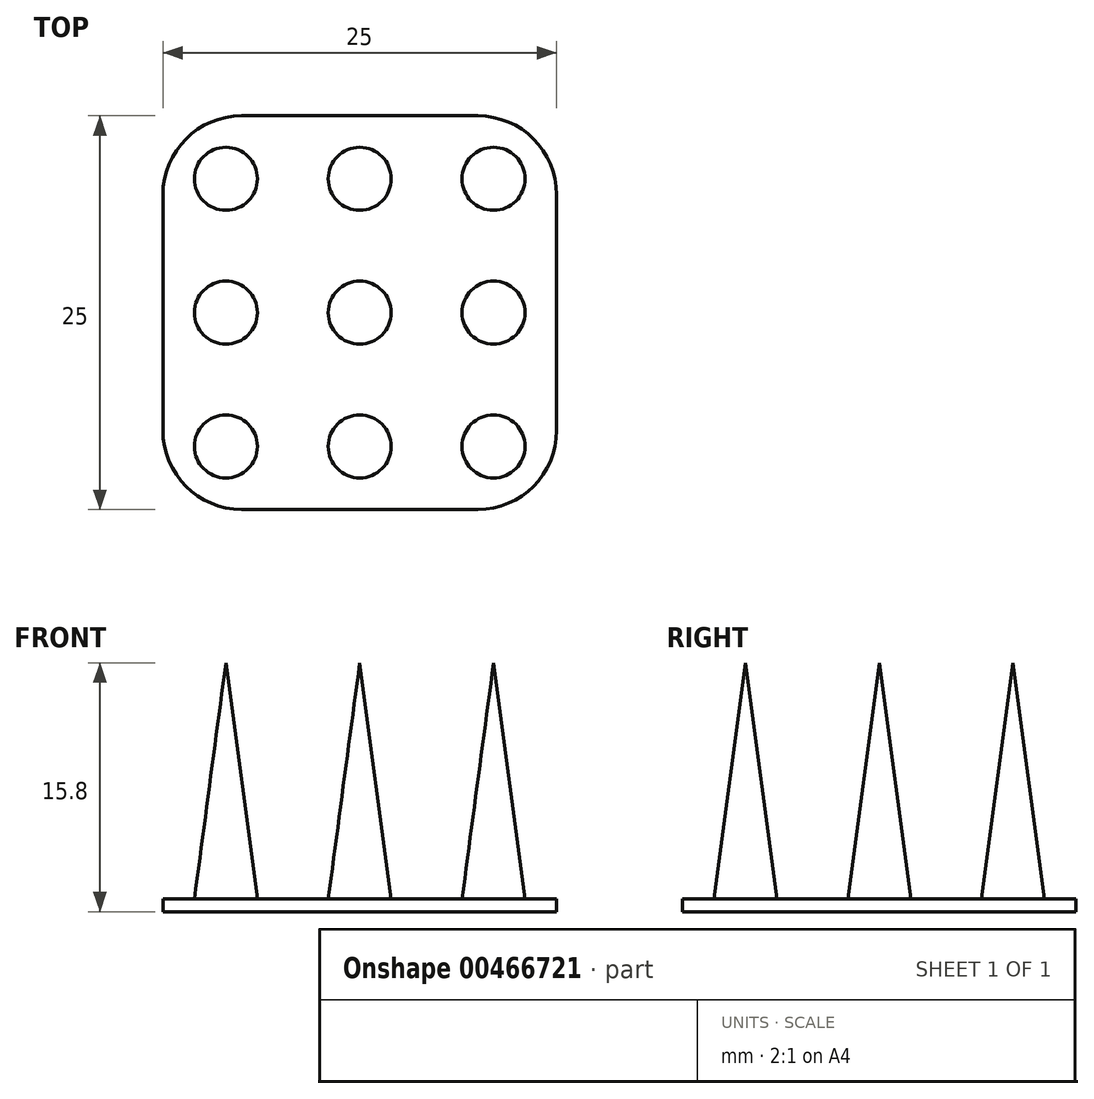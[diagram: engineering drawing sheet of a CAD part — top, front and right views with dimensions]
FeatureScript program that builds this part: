
annotation { "Feature Type Name" : "Feature", "Feature Type Description" : "" }
export const myFeature = defineFeature(function(context is Context, id is Id, definition is map)
    precondition{}
    {
        {
            var Q0;
            Q0=qCreatedBy(makeId("Top.planeOp"),FACE);
            var sketch = newSketch(context, id + "F0", { "sketchPlane" : qUnion([Q0])});
            skLineSegment(sketch, "E0.bottom", {"start": v(-7.5, -12.5) * mm, "end": v(7.5, -12.5) * mm});
            skLineSegment(sketch, "E0.top", {"start": v(-7.5, 12.5) * mm, "end": v(7.5, 12.5) * mm});
            skLineSegment(sketch, "E0.left", {"start": v(-12.5, -7.5) * mm, "end": v(-12.5, 7.5) * mm});
            skLineSegment(sketch, "E0.right", {"start": v(12.5, -7.5) * mm, "end": v(12.5, 7.5) * mm});
            skPoint(sketch, "E1.visualSharp", {"position": v(-12.5, 12.5) * mm});
            skArc(sketch, "E1.filletArc", {"start": v(-7.5, 12.5) * mm, "mid": v(-11.04, 11.04) * mm, "end": v(-12.5, 7.5) * mm});
            skPoint(sketch, "E2.visualSharp", {"position": v(12.5, 12.5) * mm});
            skArc(sketch, "E2.filletArc", {"start": v(12.5, 7.5) * mm, "mid": v(11.04, 11.04) * mm, "end": v(7.5, 12.5) * mm});
            skPoint(sketch, "E3.visualSharp", {"position": v(12.5, -12.5) * mm});
            skArc(sketch, "E3.filletArc", {"start": v(7.5, -12.5) * mm, "mid": v(11.04, -11.04) * mm, "end": v(12.5, -7.5) * mm});
            skPoint(sketch, "E4.visualSharp", {"position": v(-12.5, -12.5) * mm});
            skArc(sketch, "E4.filletArc", {"start": v(-12.5, -7.5) * mm, "mid": v(-11.04, -11.04) * mm, "end": v(-7.5, -12.5) * mm});
            skSolve(sketch);
        }
        {
            var Q0;
            Q0 = qSketchRegion(id + "F0", true);
            extrude(context, id + "F1", {"entities" : qUnion([Q0]), "depth" : .8 * mm});
        }
        {
            var Q0;
            Q0=makeQuery(id+"F1.opExtrude","CAP_FACE",FACE,{"disambiguationData":[OSD([sQuery(id+"F0.wireOp",EDGE,"E0.bottom"),sQuery(id+"F0.wireOp",EDGE,"E0.top"),sQuery(id+"F0.wireOp",EDGE,"E0.left"),sQuery(id+"F0.wireOp",EDGE,"E0.right"),sQuery(id+"F0.wireOp",EDGE,"E1.filletArc"),sQuery(id+"F0.wireOp",EDGE,"E2.filletArc"),sQuery(id+"F0.wireOp",EDGE,"E3.filletArc"),sQuery(id+"F0.wireOp",EDGE,"E4.filletArc")])],"isStart":false});
            var sketch = newSketch(context, id + "F2", { "sketchPlane" : qUnion([Q0])});
            skCircle(sketch, "E5", {"center": v(-8.5, -8.5) * mm, "radius": 2 * mm});
            skCircle(sketch, "E6.0.1.0", {"center": v(-8.5, 0) * mm, "radius": 2 * mm});
            skCircle(sketch, "E6.0.2.0", {"center": v(-8.5, 8.5) * mm, "radius": 2 * mm});
            skCircle(sketch, "E6.1.0.0", {"center": v(0, -8.5) * mm, "radius": 2 * mm});
            skCircle(sketch, "E6.1.1.0", {"center": v(0, 0) * mm, "radius": 2 * mm});
            skCircle(sketch, "E6.1.2.0", {"center": v(0, 8.5) * mm, "radius": 2 * mm});
            skCircle(sketch, "E6.2.0.0", {"center": v(8.5, -8.5) * mm, "radius": 2 * mm});
            skCircle(sketch, "E6.2.1.0", {"center": v(8.5, 0) * mm, "radius": 2 * mm});
            skCircle(sketch, "E6.2.2.0", {"center": v(8.5, 8.5) * mm, "radius": 2 * mm});
            skLineSegment(sketch, "E6.direction1", {"start": v(-8.5, -8.5) * mm, "end": v(0, -8.5) * mm, "construction": true});
            skLineSegment(sketch, "E6.direction2", {"start": v(-8.5, -8.5) * mm, "end": v(-8.5, 0) * mm, "construction": true});
            skSolve(sketch);
        }
        {
            var Q0;
            Q0 = qSketchRegion(id + "F2", true);
            extrude(context, id + "F3", {"entities" : qUnion([Q0]), "operationType" : NewBodyOperationType.ADD, "depth" : 15 * mm});
        }
        {
            var Q0;
            Q0=makeQuery(id+"F3.opExtrude","CAP_EDGE",EDGE,{"disambiguationData":[OSD([sQuery(id+"F2.wireOp",EDGE,"E5")])],"isStart":false});
            var Q1;
            Q1=makeQuery(id+"F3.opExtrude","CAP_EDGE",EDGE,{"disambiguationData":[OSD([sQuery(id+"F2.wireOp",EDGE,"E6.0.1.0")])],"isStart":false});
            var Q2;
            Q2=makeQuery(id+"F3.opExtrude","CAP_EDGE",EDGE,{"disambiguationData":[OSD([sQuery(id+"F2.wireOp",EDGE,"E6.0.2.0")])],"isStart":false});
            var Q3;
            Q3=makeQuery(id+"F3.opExtrude","CAP_EDGE",EDGE,{"disambiguationData":[OSD([sQuery(id+"F2.wireOp",EDGE,"E6.1.2.0")])],"isStart":false});
            var Q4;
            Q4=makeQuery(id+"F3.opExtrude","CAP_EDGE",EDGE,{"disambiguationData":[OSD([sQuery(id+"F2.wireOp",EDGE,"E6.1.1.0")])],"isStart":false});
            var Q5;
            Q5=makeQuery(id+"F3.opExtrude","CAP_EDGE",EDGE,{"disambiguationData":[OSD([sQuery(id+"F2.wireOp",EDGE,"E6.1.0.0")])],"isStart":false});
            var Q6;
            Q6=makeQuery(id+"F3.opExtrude","CAP_EDGE",EDGE,{"disambiguationData":[OSD([sQuery(id+"F2.wireOp",EDGE,"E6.2.0.0")])],"isStart":false});
            var Q7;
            Q7=makeQuery(id+"F3.opExtrude","CAP_EDGE",EDGE,{"disambiguationData":[OSD([sQuery(id+"F2.wireOp",EDGE,"E6.2.1.0")])],"isStart":false});
            var Q8;
            Q8=makeQuery(id+"F3.opExtrude","CAP_EDGE",EDGE,{"disambiguationData":[OSD([sQuery(id+"F2.wireOp",EDGE,"E6.2.2.0")])],"isStart":false});
            chamfer(context, id + "F4", {"entities" : qUnion([Q0, Q1, Q2, Q3, Q4, Q5, Q6, Q7, Q8]), "chamferType" : ChamferType.TWO_OFFSETS, "width1" : 2 * mm, "oppositeDirection" : false, "width2" : 15 * mm, "tangentPropagation" : true});
        }
    });
